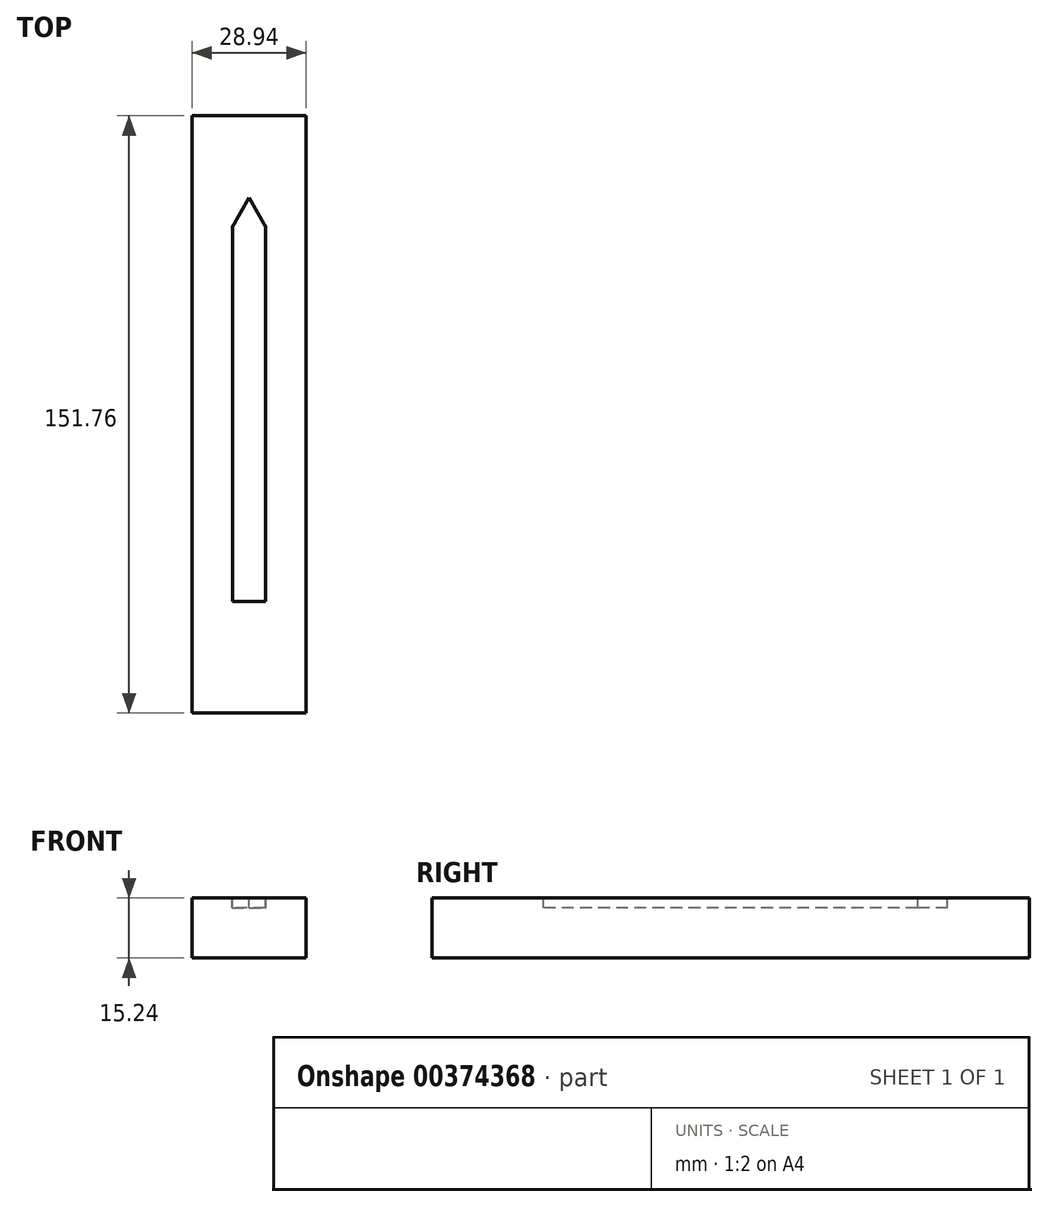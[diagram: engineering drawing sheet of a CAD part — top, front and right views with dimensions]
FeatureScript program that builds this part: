
annotation { "Feature Type Name" : "Feature", "Feature Type Description" : "" }
export const myFeature = defineFeature(function(context is Context, id is Id, definition is map)
    precondition{}
    {
        {
            var Q0;
            Q0=qCreatedBy(makeId("Top.planeOp"),FACE);
            var sketch = newSketch(context, id + "F0", { "sketchPlane" : qUnion([Q0])});
            skLineSegment(sketch, "E0.bottom", {"start": v(14.47, 75.88) * mm, "end": v(-14.47, 75.88) * mm});
            skLineSegment(sketch, "E0.top", {"start": v(14.47, -75.88) * mm, "end": v(-14.47, -75.88) * mm});
            skLineSegment(sketch, "E0.left", {"start": v(14.47, 75.88) * mm, "end": v(14.47, -75.88) * mm});
            skLineSegment(sketch, "E0.right", {"start": v(-14.47, 75.88) * mm, "end": v(-14.47, -75.88) * mm});
            skPoint(sketch, "E0.middle", {"position": v(0, 0) * mm});
            skSolve(sketch);
        }
        {
            var Q0;
            Q0=makeQuery(id+"F0.imprint","IMPRINT",FACE,{"disambiguationData":[TD([[makeQuery(id+"F0.imprint","IMPRINT",EDGE,{"derivedFrom":sQuery(id+"F0.wireOp",EDGE,"E0.bottom")}),1.0]])]});
            extrude(context, id + "F1", {"entities" : qUnion([Q0]), "depth" : 15.24 * mm});
        }
        {
            var Q0;
            Q0=makeQuery(id+"F1.opExtrude","CAP_FACE",FACE,{"disambiguationData":[OSD([sQuery(id+"F0.wireOp",EDGE,"E0.bottom"),sQuery(id+"F0.wireOp",EDGE,"E0.top"),sQuery(id+"F0.wireOp",EDGE,"E0.left"),sQuery(id+"F0.wireOp",EDGE,"E0.right")])],"isStart":false});
            var sketch = newSketch(context, id + "F2", { "sketchPlane" : qUnion([Q0])});
            skLineSegment(sketch, "E1.bottom", {"start": v(4.13, 47.53) * mm, "end": v(-4.13, 47.53) * mm});
            skLineSegment(sketch, "E1.top", {"start": v(4.13, -47.53) * mm, "end": v(-4.13, -47.53) * mm});
            skLineSegment(sketch, "E1.left", {"start": v(4.13, 47.53) * mm, "end": v(4.13, -47.53) * mm});
            skLineSegment(sketch, "E1.right", {"start": v(-4.13, 47.53) * mm, "end": v(-4.13, -47.53) * mm});
            skPoint(sketch, "E1.middle", {"position": v(0, 0) * mm});
            skLineSegment(sketch, "E2.bottom", {"start": v(1.32, -47.53) * mm, "end": v(-1.32, -47.53) * mm});
            skLineSegment(sketch, "E2.top", {"start": v(1.32, -70.56) * mm, "end": v(-1.32, -70.56) * mm});
            skLineSegment(sketch, "E2.left", {"start": v(1.32, -47.53) * mm, "end": v(1.32, -70.56) * mm});
            skLineSegment(sketch, "E2.right", {"start": v(-1.32, -47.53) * mm, "end": v(-1.32, -70.56) * mm});
            skPoint(sketch, "E2.middle", {"position": v(0, -59.05) * mm});
            skCircle(sketch, "E3.cCircle", {"center": v(0, 50.06) * mm, "radius": 2.52 * mm, "construction": true});
            skPoint(sketch, "E3.cCircle.centerSnap0", {"position": v(0, 47.53) * mm});
            skLineSegment(sketch, "E3.0", {"start": v(4.37, 47.53) * mm, "end": v(-4.37, 47.53) * mm});
            skLineSegment(sketch, "E3.1", {"start": v(-4.37, 47.53) * mm, "end": v(0, 55.1) * mm});
            skLineSegment(sketch, "E3.2", {"start": v(0, 55.1) * mm, "end": v(4.37, 47.53) * mm});
            skPoint(sketch, "E3.0.midPoint", {"position": v(0, 47.53) * mm});
            skSolve(sketch);
        }
        {
            var Q0;
            {var subQ0=sQuery(id+"F2.wireOp",EDGE,"E3.1");Q0=makeQuery(id+"F2.imprint","IMPRINT",FACE,{"disambiguationData":[TD([[makeQuery(id+"F2.imprint","IMPRINT",EDGE,{"derivedFrom":subQ0}),-1.0]])]});}
            var Q1;
            {var subQ1=sQuery(id+"F2.wireOp",EDGE,"E1.left");Q1=makeQuery(id+"F2.imprint","IMPRINT",FACE,{"disambiguationData":[TD([[makeQuery(id+"F2.imprint","IMPRINT",EDGE,{"derivedFrom":subQ1}),-1.0]])]});}
            var Q2;
            Q2=makeQuery(id+"F2.imprint","IMPRINT",FACE,{"disambiguationData":[TD([[makeQuery(id+"F2.imprint","IMPRINT",EDGE,{"derivedFrom":sQuery(id+"F2.wireOp",EDGE,"E2.bottom")}),1.0]])]});
            extrude(context, id + "F3", {"entities" : qUnion([Q0, Q1, Q2]), "operationType" : NewBodyOperationType.REMOVE, "oppositeDirection" : true, "depth" : 2.54 * mm});
        }
    });
